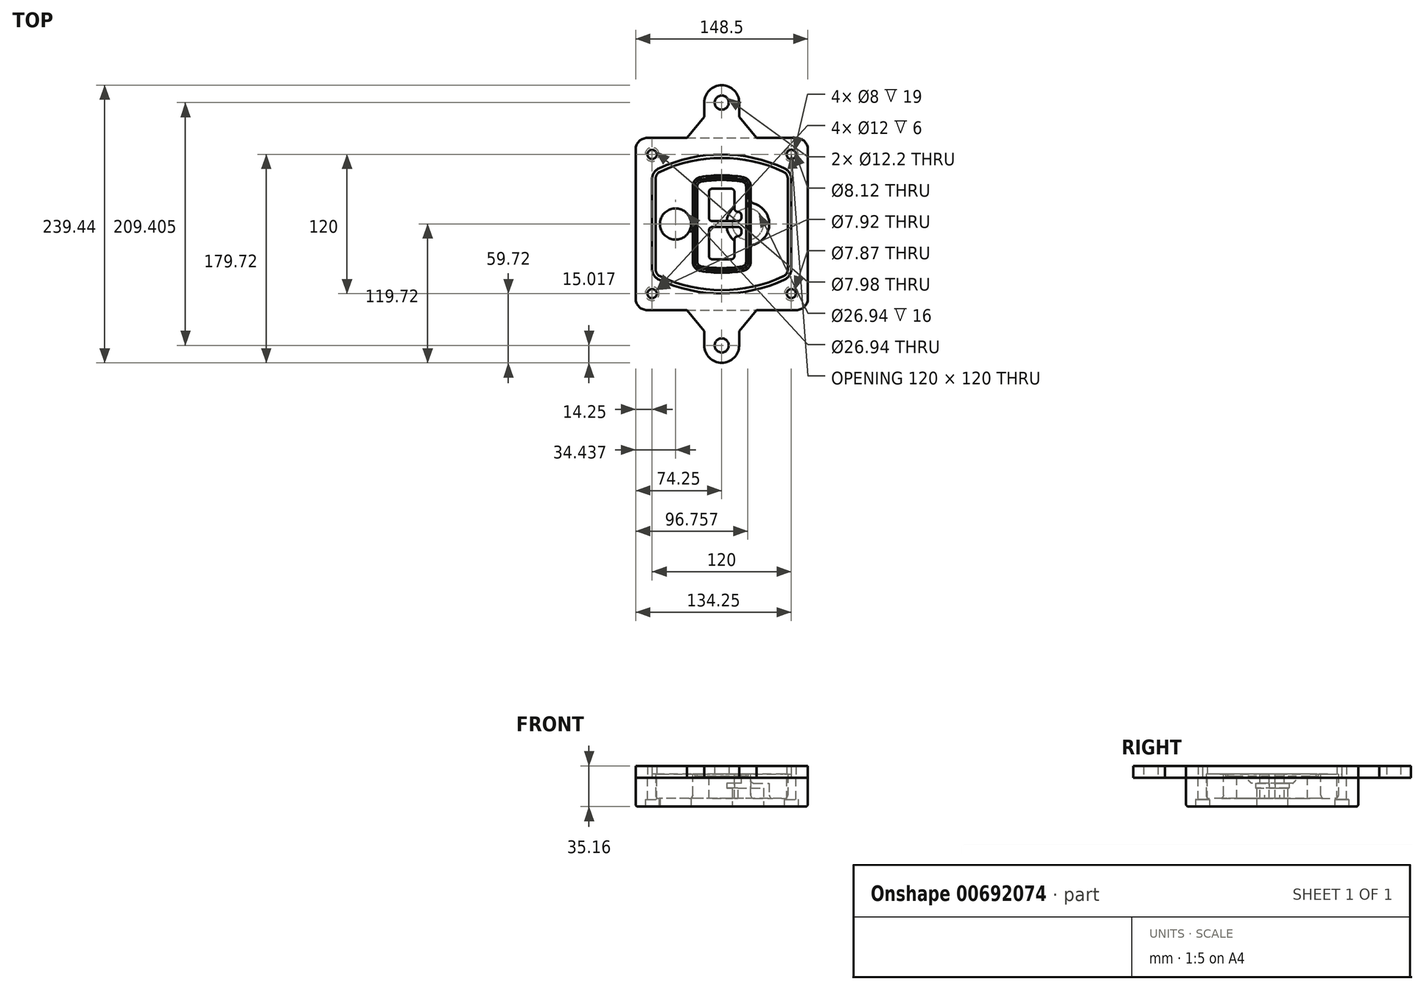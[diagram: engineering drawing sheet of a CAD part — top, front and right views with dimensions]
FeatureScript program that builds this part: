
annotation { "Feature Type Name" : "Feature", "Feature Type Description" : "" }
export const myFeature = defineFeature(function(context is Context, id is Id, definition is map)
    precondition{}
    {
        {
            var Q0;
            Q0=qCreatedBy(makeId("Top.planeOp"),FACE);
            var sketch = newSketch(context, id + "F0", { "sketchPlane" : qUnion([Q0])});
            skPoint(sketch, "E0.rect.middle", {"position": v(0, 0) * mm});
            skLineSegment(sketch, "E1.bottom", {"start": v(-64.25, -74.25) * mm, "end": v(64.25, -74.25) * mm});
            skLineSegment(sketch, "E1.top", {"start": v(-64.25, 74.25) * mm, "end": v(64.25, 74.25) * mm});
            skLineSegment(sketch, "E1.left", {"start": v(-74.25, -64.25) * mm, "end": v(-74.25, 64.25) * mm});
            skLineSegment(sketch, "E1.right", {"start": v(74.25, -64.25) * mm, "end": v(74.25, 64.25) * mm});
            skLineSegment(sketch, "E2", {"start": v(-74.25, 74.25) * mm, "end": v(74.25, -74.25) * mm, "construction": true});
            skLineSegment(sketch, "E3", {"start": v(74.25, 74.25) * mm, "end": v(-74.25, -74.25) * mm, "construction": true});
            skCircle(sketch, "E4", {"center": v(-60, 60) * mm, "radius": 4 * mm});
            skCircle(sketch, "E5", {"center": v(60, 60) * mm, "radius": 4 * mm});
            skCircle(sketch, "E6", {"center": v(60, -60) * mm, "radius": 4 * mm});
            skCircle(sketch, "E7", {"center": v(-60, -60) * mm, "radius": 4 * mm});
            skLineSegment(sketch, "E8", {"start": v(-60, 60) * mm, "end": v(60, 60) * mm, "construction": true});
            skLineSegment(sketch, "E9", {"start": v(60, 60) * mm, "end": v(60, -60) * mm, "construction": true});
            skLineSegment(sketch, "E10", {"start": v(60, -60) * mm, "end": v(-60, -60) * mm, "construction": true});
            skLineSegment(sketch, "E11", {"start": v(-60, -60) * mm, "end": v(-60, 60) * mm, "construction": true});
            skLineSegment(sketch, "E12", {"start": v(-60, 38.83) * mm, "end": v(-60, -38.83) * mm});
            skLineSegment(sketch, "E13", {"start": v(60, 38.83) * mm, "end": v(60, -38.83) * mm});
            skArc(sketch, "E14", {"start": v(54.26, 47.88) * mm, "mid": v(0, 60) * mm, "end": v(-54.26, 47.88) * mm});
            skArc(sketch, "E15", {"start": v(-54.26, -47.88) * mm, "mid": v(0, -60) * mm, "end": v(54.26, -47.88) * mm});
            skLineSegment(sketch, "E16", {"start": v(-60, 0) * mm, "end": v(60, 0) * mm, "construction": true});
            skPoint(sketch, "E17.visualSharp", {"position": v(-60, -45) * mm});
            skArc(sketch, "E17.filletArc", {"start": v(-60, -38.83) * mm, "mid": v(-58.44, -44.2) * mm, "end": v(-54.26, -47.88) * mm});
            skPoint(sketch, "E18.visualSharp", {"position": v(-60, 45) * mm});
            skArc(sketch, "E18.filletArc", {"start": v(-54.26, 47.88) * mm, "mid": v(-58.44, 44.2) * mm, "end": v(-60, 38.83) * mm});
            skPoint(sketch, "E19.visualSharp", {"position": v(60, 45) * mm});
            skArc(sketch, "E19.filletArc", {"start": v(60, 38.83) * mm, "mid": v(58.44, 44.2) * mm, "end": v(54.26, 47.88) * mm});
            skPoint(sketch, "E20.visualSharp", {"position": v(60, -45) * mm});
            skArc(sketch, "E20.filletArc", {"start": v(54.26, -47.88) * mm, "mid": v(58.44, -44.2) * mm, "end": v(60, -38.83) * mm});
            skPoint(sketch, "E21.visualSharp", {"position": v(-74.25, 74.25) * mm});
            skArc(sketch, "E21.filletArc", {"start": v(-64.25, 74.25) * mm, "mid": v(-71.32, 71.32) * mm, "end": v(-74.25, 64.25) * mm});
            skPoint(sketch, "E22.visualSharp", {"position": v(74.25, 74.25) * mm});
            skArc(sketch, "E22.filletArc", {"start": v(74.25, 64.25) * mm, "mid": v(71.32, 71.32) * mm, "end": v(64.25, 74.25) * mm});
            skPoint(sketch, "E23.visualSharp", {"position": v(74.25, -74.25) * mm});
            skArc(sketch, "E23.filletArc", {"start": v(64.25, -74.25) * mm, "mid": v(71.32, -71.32) * mm, "end": v(74.25, -64.25) * mm});
            skPoint(sketch, "E24.visualSharp", {"position": v(-74.25, -74.25) * mm});
            skArc(sketch, "E24.filletArc", {"start": v(-74.25, -64.25) * mm, "mid": v(-71.32, -71.32) * mm, "end": v(-64.25, -74.25) * mm});
            skArc(sketch, "E25.0", {"start": v(57, 38.83) * mm, "mid": v(55.9, 42.58) * mm, "end": v(52.98, 45.17) * mm});
            skLineSegment(sketch, "E25.1", {"start": v(57, 38.83) * mm, "end": v(57, -38.83) * mm});
            skArc(sketch, "E25.2", {"start": v(52.98, -45.17) * mm, "mid": v(55.9, -42.58) * mm, "end": v(57, -38.83) * mm});
            skArc(sketch, "E25.3", {"start": v(-52.98, -45.17) * mm, "mid": v(0, -57) * mm, "end": v(52.98, -45.17) * mm});
            skArc(sketch, "E25.4", {"start": v(-57, -38.83) * mm, "mid": v(-55.9, -42.58) * mm, "end": v(-52.98, -45.17) * mm});
            skArc(sketch, "E25.5", {"start": v(52.98, 45.17) * mm, "mid": v(0, 57) * mm, "end": v(-52.98, 45.17) * mm});
            skLineSegment(sketch, "E25.6", {"start": v(-57, 38.83) * mm, "end": v(-57, -38.83) * mm});
            skArc(sketch, "E25.7", {"start": v(-52.98, 45.17) * mm, "mid": v(-55.9, 42.58) * mm, "end": v(-57, 38.83) * mm});
            skArc(sketch, "E26.0", {"start": v(-55.96, 51.5) * mm, "mid": v(-61.82, 46.33) * mm, "end": v(-64, 38.83) * mm});
            skArc(sketch, "E26.1", {"start": v(55.96, 51.5) * mm, "mid": v(0, 64) * mm, "end": v(-55.96, 51.5) * mm});
            skArc(sketch, "E26.2", {"start": v(64, 38.83) * mm, "mid": v(61.82, 46.33) * mm, "end": v(55.96, 51.5) * mm});
            skLineSegment(sketch, "E26.3", {"start": v(64, 38.83) * mm, "end": v(64, -38.83) * mm});
            skArc(sketch, "E26.4", {"start": v(55.96, -51.5) * mm, "mid": v(61.82, -46.33) * mm, "end": v(64, -38.83) * mm});
            skLineSegment(sketch, "E26.5", {"start": v(-64, 38.83) * mm, "end": v(-64, -38.83) * mm});
            skArc(sketch, "E26.6", {"start": v(-55.96, -51.5) * mm, "mid": v(0, -64) * mm, "end": v(55.96, -51.5) * mm});
            skArc(sketch, "E26.7", {"start": v(-64, -38.83) * mm, "mid": v(-61.82, -46.33) * mm, "end": v(-55.96, -51.5) * mm});
            skSolve(sketch);
        }
        {
            var Q0;
            Q0=makeQuery(id+"F0.imprint","IMPRINT",FACE,{"disambiguationData":[TD([[makeQuery(id+"F0.imprint","IMPRINT",EDGE,{"derivedFrom":sQuery(id+"F0.wireOp",EDGE,"E1.bottom")}),1.0]])]});
            var Q1;
            Q1=makeQuery(id+"F0.imprint","IMPRINT",FACE,{"disambiguationData":[TD([[makeQuery(id+"F0.imprint","IMPRINT",EDGE,{"derivedFrom":sQuery(id+"F0.wireOp",EDGE,"E12")}),1.0]])]});
            var Q2;
            Q2=makeQuery(id+"F0.imprint","IMPRINT",FACE,{"disambiguationData":[TD([[makeQuery(id+"F0.imprint","IMPRINT",EDGE,{"derivedFrom":sQuery(id+"F0.wireOp",EDGE,"E25.0")}),1.0]])]});
            var Q3;
            Q3=makeQuery(id+"F0.imprint","IMPRINT",FACE,{"disambiguationData":[TD([[makeQuery(id+"F0.imprint","IMPRINT",EDGE,{"derivedFrom":sQuery(id+"F0.wireOp",EDGE,"E12")}),-1.0]])]});
            extrude(context, id + "F1", {"entities" : qUnion([Q0, Q1, Q2, Q3]), "oppositeDirection" : true, "depth" : 25 * mm});
        }
        {
            var Q0;
            Q0=makeQuery(id+"F0.imprint","IMPRINT",FACE,{"disambiguationData":[TD([[makeQuery(id+"F0.imprint","IMPRINT",EDGE,{"derivedFrom":sQuery(id+"F0.wireOp",EDGE,"E12")}),1.0]])]});
            extrude(context, id + "F2", {"entities" : qUnion([Q0]), "operationType" : NewBodyOperationType.ADD, "depth" : 3 * mm});
        }
        {
            var Q0;
            Q0=makeQuery(id+"F0.imprint","IMPRINT",FACE,{"disambiguationData":[TD([[makeQuery(id+"F0.imprint","IMPRINT",EDGE,{"derivedFrom":sQuery(id+"F0.wireOp",EDGE,"E25.0")}),1.0]])]});
            extrude(context, id + "F3", {"entities" : qUnion([Q0]), "operationType" : NewBodyOperationType.REMOVE, "oppositeDirection" : true, "depth" : 18 * mm});
        }
        {
            var Q0;
            Q0=makeQuery(id+"F2.opExtrude","CAP_FACE",FACE,{"disambiguationData":[OSD([sQuery(id+"F0.wireOp",EDGE,"E12"),sQuery(id+"F0.wireOp",EDGE,"E13"),sQuery(id+"F0.wireOp",EDGE,"E14"),sQuery(id+"F0.wireOp",EDGE,"E15"),sQuery(id+"F0.wireOp",EDGE,"E17.filletArc"),sQuery(id+"F0.wireOp",EDGE,"E18.filletArc"),sQuery(id+"F0.wireOp",EDGE,"E19.filletArc"),sQuery(id+"F0.wireOp",EDGE,"E20.filletArc"),sQuery(id+"F0.wireOp",EDGE,"E25.0"),sQuery(id+"F0.wireOp",EDGE,"E25.1"),sQuery(id+"F0.wireOp",EDGE,"E25.2"),sQuery(id+"F0.wireOp",EDGE,"E25.3"),sQuery(id+"F0.wireOp",EDGE,"E25.4"),sQuery(id+"F0.wireOp",EDGE,"E25.5"),sQuery(id+"F0.wireOp",EDGE,"E25.6"),sQuery(id+"F0.wireOp",EDGE,"E25.7")])],"isStart":false});
            var sketch = newSketch(context, id + "F4", { "sketchPlane" : qUnion([Q0])});
            skArc(sketch, "E27.0", {"start": v(-18.34, -40.45) * mm, "mid": v(0, -42) * mm, "end": v(18.34, -40.45) * mm});
            skArc(sketch, "E28.0", {"start": v(18.34, 40.45) * mm, "mid": v(0, 42) * mm, "end": v(-18.34, 40.45) * mm});
            skLineSegment(sketch, "E29", {"start": v(-25, 32.57) * mm, "end": v(-25, -32.57) * mm});
            skLineSegment(sketch, "E30", {"start": v(25, 32.57) * mm, "end": v(25, -32.57) * mm});
            skLineSegment(sketch, "E31", {"start": v(-25, 39.1) * mm, "end": v(25, 39.1) * mm, "construction": true});
            skLineSegment(sketch, "E32", {"start": v(-25, -39.1) * mm, "end": v(25, -39.1) * mm, "construction": true});
            skPoint(sketch, "E33.visualSharp", {"position": v(-25, 39.1) * mm});
            skArc(sketch, "E33.filletArc", {"start": v(-18.34, 40.45) * mm, "mid": v(-23.11, 37.73) * mm, "end": v(-25, 32.57) * mm});
            skPoint(sketch, "E34.visualSharp", {"position": v(25, 39.1) * mm});
            skArc(sketch, "E34.filletArc", {"start": v(25, 32.57) * mm, "mid": v(23.11, 37.73) * mm, "end": v(18.34, 40.45) * mm});
            skPoint(sketch, "E35.visualSharp", {"position": v(25, -39.1) * mm});
            skArc(sketch, "E35.filletArc", {"start": v(18.34, -40.45) * mm, "mid": v(23.11, -37.73) * mm, "end": v(25, -32.57) * mm});
            skPoint(sketch, "E36.visualSharp", {"position": v(-25, -39.1) * mm});
            skArc(sketch, "E36.filletArc", {"start": v(-25, -32.57) * mm, "mid": v(-23.11, -37.73) * mm, "end": v(-18.34, -40.45) * mm});
            skArc(sketch, "E37.0", {"start": v(52.98, 45.17) * mm, "mid": v(0, 57) * mm, "end": v(-52.98, 45.17) * mm});
            skArc(sketch, "E37.1", {"start": v(-52.98, 45.17) * mm, "mid": v(-55.9, 42.58) * mm, "end": v(-57, 38.83) * mm});
            skLineSegment(sketch, "E37.2", {"start": v(-57, 38.83) * mm, "end": v(-57, -38.83) * mm});
            skArc(sketch, "E37.3", {"start": v(-57, -38.83) * mm, "mid": v(-55.9, -42.58) * mm, "end": v(-52.98, -45.17) * mm});
            skArc(sketch, "E37.4", {"start": v(-52.98, -45.17) * mm, "mid": v(0, -57) * mm, "end": v(52.98, -45.17) * mm});
            skArc(sketch, "E37.5", {"start": v(52.98, -45.17) * mm, "mid": v(55.9, -42.58) * mm, "end": v(57, -38.83) * mm});
            skLineSegment(sketch, "E37.6", {"start": v(57, 38.83) * mm, "end": v(57, -38.83) * mm});
            skArc(sketch, "E37.7", {"start": v(57, 38.83) * mm, "mid": v(55.9, 42.58) * mm, "end": v(52.98, 45.17) * mm});
            skLineSegment(sketch, "E38.0", {"start": v(23, 32.57) * mm, "end": v(23, -32.57) * mm});
            skArc(sketch, "E38.1", {"start": v(18, -38.48) * mm, "mid": v(21.58, -36.44) * mm, "end": v(23, -32.57) * mm});
            skArc(sketch, "E38.2", {"start": v(-18, -38.48) * mm, "mid": v(0, -40) * mm, "end": v(18, -38.48) * mm});
            skArc(sketch, "E38.3", {"start": v(-23, -32.57) * mm, "mid": v(-21.58, -36.44) * mm, "end": v(-18, -38.48) * mm});
            skLineSegment(sketch, "E38.4", {"start": v(-23, 32.57) * mm, "end": v(-23, -32.57) * mm});
            skArc(sketch, "E38.5", {"start": v(23, 32.57) * mm, "mid": v(21.58, 36.44) * mm, "end": v(18, 38.48) * mm});
            skArc(sketch, "E38.6", {"start": v(-18, 38.48) * mm, "mid": v(-21.58, 36.44) * mm, "end": v(-23, 32.57) * mm});
            skArc(sketch, "E38.7", {"start": v(18, 38.48) * mm, "mid": v(0, 40) * mm, "end": v(-18, 38.48) * mm});
            skArc(sketch, "E39.0", {"start": v(21, 32.57) * mm, "mid": v(20.06, 35.15) * mm, "end": v(17.67, 36.5) * mm});
            skLineSegment(sketch, "E39.1", {"start": v(21, 32.57) * mm, "end": v(21, -32.57) * mm});
            skArc(sketch, "E39.2", {"start": v(17.67, -36.5) * mm, "mid": v(20.06, -35.15) * mm, "end": v(21, -32.57) * mm});
            skArc(sketch, "E39.3", {"start": v(-17.67, -36.5) * mm, "mid": v(0, -38) * mm, "end": v(17.67, -36.5) * mm});
            skArc(sketch, "E39.4", {"start": v(-21, -32.57) * mm, "mid": v(-20.06, -35.15) * mm, "end": v(-17.67, -36.5) * mm});
            skArc(sketch, "E39.5", {"start": v(17.67, 36.5) * mm, "mid": v(0, 38) * mm, "end": v(-17.67, 36.5) * mm});
            skLineSegment(sketch, "E39.6", {"start": v(-21, 32.57) * mm, "end": v(-21, -32.57) * mm});
            skArc(sketch, "E39.7", {"start": v(-17.67, 36.5) * mm, "mid": v(-20.06, 35.15) * mm, "end": v(-21, 32.57) * mm});
            skLineSegment(sketch, "E40", {"start": v(-25, 0) * mm, "end": v(25, 0) * mm, "construction": true});
            skLineSegment(sketch, "E41", {"start": v(-11, 5.5) * mm, "end": v(-11, 27.5) * mm});
            skLineSegment(sketch, "E42", {"start": v(-8, 30.5) * mm, "end": v(8, 30.5) * mm});
            skLineSegment(sketch, "E43", {"start": v(11, 27.5) * mm, "end": v(11, 13.5) * mm});
            skLineSegment(sketch, "E44", {"start": v(14, 10.5) * mm, "end": v(14, 10.5) * mm});
            skLineSegment(sketch, "E45", {"start": v(17, 7.5) * mm, "end": v(17, 5.5) * mm});
            skLineSegment(sketch, "E46", {"start": v(14, 2.5) * mm, "end": v(-8, 2.5) * mm});
            skPoint(sketch, "E47.visualSharp", {"position": v(-11, 30.5) * mm});
            skArc(sketch, "E47.filletArc", {"start": v(-8, 30.5) * mm, "mid": v(-10.12, 29.62) * mm, "end": v(-11, 27.5) * mm});
            skPoint(sketch, "E48.visualSharp", {"position": v(11, 30.5) * mm});
            skArc(sketch, "E48.filletArc", {"start": v(11, 27.5) * mm, "mid": v(10.12, 29.62) * mm, "end": v(8, 30.5) * mm});
            skPoint(sketch, "E49.visualSharp", {"position": v(11, 10.5) * mm});
            skArc(sketch, "E49.filletArc", {"start": v(11, 13.5) * mm, "mid": v(11.88, 11.38) * mm, "end": v(14, 10.5) * mm});
            skPoint(sketch, "E50.visualSharp", {"position": v(17, 10.5) * mm});
            skArc(sketch, "E50.filletArc", {"start": v(17, 7.5) * mm, "mid": v(16.12, 9.62) * mm, "end": v(14, 10.5) * mm});
            skPoint(sketch, "E51.visualSharp", {"position": v(17, 2.5) * mm});
            skArc(sketch, "E51.filletArc", {"start": v(14, 2.5) * mm, "mid": v(16.12, 3.38) * mm, "end": v(17, 5.5) * mm});
            skPoint(sketch, "E52.visualSharp", {"position": v(-11, 2.5) * mm});
            skArc(sketch, "E52.filletArc", {"start": v(-11, 5.5) * mm, "mid": v(-10.12, 3.38) * mm, "end": v(-8, 2.5) * mm});
            skLineSegment(sketch, "E53.0.MirrorCS", {"start": v(14, -2.5) * mm, "end": v(-8, -2.5) * mm});
            skArc(sketch, "E54.0.MirrorCS", {"start": v(-11, -5.5) * mm, "mid": v(-10.12, -3.38) * mm, "end": v(-8, -2.5) * mm});
            skLineSegment(sketch, "E55.0.MirrorCS", {"start": v(-11, -5.5) * mm, "end": v(-11, -27.5) * mm});
            skArc(sketch, "E56.0.MirrorCS", {"start": v(-8, -30.5) * mm, "mid": v(-10.12, -29.62) * mm, "end": v(-11, -27.5) * mm});
            skLineSegment(sketch, "E57.0.MirrorCS", {"start": v(-8, -30.5) * mm, "end": v(8, -30.5) * mm});
            skArc(sketch, "E58.0.MirrorCS", {"start": v(11, -27.5) * mm, "mid": v(10.12, -29.62) * mm, "end": v(8, -30.5) * mm});
            skLineSegment(sketch, "E59.0.MirrorCS", {"start": v(11, -27.5) * mm, "end": v(11, -13.5) * mm});
            skArc(sketch, "E60.0.MirrorCS", {"start": v(11, -13.5) * mm, "mid": v(11.88, -11.38) * mm, "end": v(14, -10.5) * mm});
            skArc(sketch, "E61.0.MirrorCS", {"start": v(17, -7.5) * mm, "mid": v(16.12, -9.62) * mm, "end": v(14, -10.5) * mm});
            skLineSegment(sketch, "E62.0.MirrorCS", {"start": v(17, -7.5) * mm, "end": v(17, -5.5) * mm});
            skArc(sketch, "E63.0.MirrorCS", {"start": v(14, -2.5) * mm, "mid": v(16.12, -3.38) * mm, "end": v(17, -5.5) * mm});
            skSolve(sketch);
        }
        {
            var Q0;
            Q0=makeQuery(id+"F4.imprint","IMPRINT",FACE,{"disambiguationData":[TD([[makeQuery(id+"F4.imprint","IMPRINT",EDGE,{"derivedFrom":sQuery(id+"F4.wireOp",EDGE,"E27.0")}),1.0]])]});
            var Q1;
            Q1=makeQuery(id+"F4.imprint","IMPRINT",FACE,{"disambiguationData":[TD([[makeQuery(id+"F4.imprint","IMPRINT",EDGE,{"derivedFrom":sQuery(id+"F4.wireOp",EDGE,"E38.0")}),-1.0]])]});
            var Q2;
            Q2=makeQuery(id+"F4.imprint","IMPRINT",FACE,{"disambiguationData":[TD([[makeQuery(id+"F4.imprint","IMPRINT",EDGE,{"derivedFrom":sQuery(id+"F4.wireOp",EDGE,"E39.0")}),1.0]])]});
            extrude(context, id + "F5", {"entities" : qUnion([Q0, Q1, Q2]), "operationType" : NewBodyOperationType.ADD, "endBound" : BoundingType.UP_TO_NEXT, "oppositeDirection" : true, "depth" : 25 * mm});
        }
        {
            var Q0;
            Q0=makeQuery(id+"F4.imprint","IMPRINT",FACE,{"disambiguationData":[TD([[makeQuery(id+"F4.imprint","IMPRINT",EDGE,{"derivedFrom":sQuery(id+"F4.wireOp",EDGE,"E38.0")}),-1.0]])]});
            extrude(context, id + "F6", {"entities" : qUnion([Q0]), "operationType" : NewBodyOperationType.REMOVE, "oppositeDirection" : true, "depth" : 2 * mm});
        }
        {
            var Q0;
            Q0=makeQuery(id+"F1.opExtrude","CAP_FACE",FACE,{"disambiguationData":[OSD([sQuery(id+"F0.wireOp",EDGE,"E1.bottom"),sQuery(id+"F0.wireOp",EDGE,"E1.top"),sQuery(id+"F0.wireOp",EDGE,"E1.left"),sQuery(id+"F0.wireOp",EDGE,"E1.right"),sQuery(id+"F0.wireOp",EDGE,"E4"),sQuery(id+"F0.wireOp",EDGE,"E5"),sQuery(id+"F0.wireOp",EDGE,"E6"),sQuery(id+"F0.wireOp",EDGE,"E7"),sQuery(id+"F0.wireOp",EDGE,"E21.filletArc"),sQuery(id+"F0.wireOp",EDGE,"E22.filletArc"),sQuery(id+"F0.wireOp",EDGE,"E23.filletArc"),sQuery(id+"F0.wireOp",EDGE,"E24.filletArc")])],"isStart":false});
            var sketch = newSketch(context, id + "F7", { "sketchPlane" : qUnion([Q0])});
            skCircle(sketch, "E64", {"center": v(22.5, 0) * mm, "radius": 13.47 * mm});
            skCircle(sketch, "E65", {"center": v(-39.81, 0) * mm, "radius": 13.47 * mm});
            skLineSegment(sketch, "E66", {"start": v(74.25, 0) * mm, "end": v(-74.25, 0) * mm});
            skCircle(sketch, "E67", {"center": v(22.5, 0) * mm, "radius": 18.47 * mm});
            skCircle(sketch, "E68", {"center": v(60, -60) * mm, "radius": 6 * mm});
            skCircle(sketch, "E69", {"center": v(-60, -60) * mm, "radius": 6 * mm});
            skCircle(sketch, "E70", {"center": v(-60, 60) * mm, "radius": 6 * mm});
            skCircle(sketch, "E71", {"center": v(60, 60) * mm, "radius": 6 * mm});
            skSolve(sketch);
        }
        {
            var Q0;
            {var subQ1=sQuery(id+"F7.wireOp",EDGE,"E66");var subQ4=sQuery(id+"F7.wireOp",EDGE,"E64");var subQ6=makeQuery(id+"F7.imprint","INTERSECT",VERTEX,{"disambiguationData":[OD(0.0)],"derivedFrom":[subQ4,subQ1]});Q0=makeQuery(id+"F7.imprint","IMPRINT",FACE,{"disambiguationData":[TD([[makeQuery(id+"F7.imprint","IMPRINT",EDGE,{"disambiguationData":[TD([[subQ6,-1.0]])],"derivedFrom":subQ4}),-1.0]])]});}
            var Q1;
            {var subQ0=sQuery(id+"F7.wireOp",EDGE,"E66");var subQ1=sQuery(id+"F7.wireOp",EDGE,"E64");var subQ3=makeQuery(id+"F7.imprint","INTERSECT",VERTEX,{"disambiguationData":[OD(0.0)],"derivedFrom":[subQ1,subQ0]});Q1=makeQuery(id+"F7.imprint","IMPRINT",FACE,{"disambiguationData":[TD([[makeQuery(id+"F7.imprint","IMPRINT",EDGE,{"disambiguationData":[TD([[subQ3,-1.0]])],"derivedFrom":subQ1}),1.0]])]});}
            var Q2;
            {var subQ0=sQuery(id+"F7.wireOp",EDGE,"E66");var subQ1=sQuery(id+"F7.wireOp",EDGE,"E64");var subQ3=makeQuery(id+"F7.imprint","INTERSECT",VERTEX,{"disambiguationData":[OD(0.0)],"derivedFrom":[subQ1,subQ0]});Q2=makeQuery(id+"F7.imprint","IMPRINT",FACE,{"disambiguationData":[TD([[makeQuery(id+"F7.imprint","IMPRINT",EDGE,{"disambiguationData":[TD([[subQ3,1.0]])],"derivedFrom":subQ1}),1.0]])]});}
            var Q3;
            {var subQ1=sQuery(id+"F7.wireOp",EDGE,"E66");var subQ4=sQuery(id+"F7.wireOp",EDGE,"E64");var subQ6=makeQuery(id+"F7.imprint","INTERSECT",VERTEX,{"disambiguationData":[OD(0.0)],"derivedFrom":[subQ4,subQ1]});Q3=makeQuery(id+"F7.imprint","IMPRINT",FACE,{"disambiguationData":[TD([[makeQuery(id+"F7.imprint","IMPRINT",EDGE,{"disambiguationData":[TD([[subQ6,1.0]])],"derivedFrom":subQ4}),-1.0]])]});}
            extrude(context, id + "F8", {"entities" : qUnion([Q0, Q1, Q2, Q3]), "operationType" : NewBodyOperationType.ADD, "oppositeDirection" : true, "depth" : 20 * mm});
        }
        {
            var Q0;
            {var subQ0=sQuery(id+"F7.wireOp",EDGE,"E66");var subQ1=sQuery(id+"F7.wireOp",EDGE,"E64");var subQ3=makeQuery(id+"F7.imprint","INTERSECT",VERTEX,{"disambiguationData":[OD(0.0)],"derivedFrom":[subQ1,subQ0]});Q0=makeQuery(id+"F7.imprint","IMPRINT",FACE,{"disambiguationData":[TD([[makeQuery(id+"F7.imprint","IMPRINT",EDGE,{"disambiguationData":[TD([[subQ3,-1.0]])],"derivedFrom":subQ1}),1.0]])]});}
            var Q1;
            {var subQ0=sQuery(id+"F7.wireOp",EDGE,"E66");var subQ1=sQuery(id+"F7.wireOp",EDGE,"E64");var subQ3=makeQuery(id+"F7.imprint","INTERSECT",VERTEX,{"disambiguationData":[OD(0.0)],"derivedFrom":[subQ1,subQ0]});Q1=makeQuery(id+"F7.imprint","IMPRINT",FACE,{"disambiguationData":[TD([[makeQuery(id+"F7.imprint","IMPRINT",EDGE,{"disambiguationData":[TD([[subQ3,1.0]])],"derivedFrom":subQ1}),1.0]])]});}
            extrude(context, id + "F9", {"entities" : qUnion([Q0, Q1]), "operationType" : NewBodyOperationType.REMOVE, "oppositeDirection" : true, "depth" : 16 * mm});
        }
        {
            var Q0;
            {var subQ0=sQuery(id+"F7.wireOp",EDGE,"E66");var subQ1=sQuery(id+"F7.wireOp",EDGE,"E65");var subQ3=makeQuery(id+"F7.imprint","INTERSECT",VERTEX,{"disambiguationData":[OD(0.0)],"derivedFrom":[subQ1,subQ0]});Q0=makeQuery(id+"F7.imprint","IMPRINT",FACE,{"disambiguationData":[TD([[makeQuery(id+"F7.imprint","IMPRINT",EDGE,{"disambiguationData":[TD([[subQ3,-1.0]])],"derivedFrom":subQ1}),1.0]])]});}
            var Q1;
            {var subQ0=sQuery(id+"F7.wireOp",EDGE,"E66");var subQ1=sQuery(id+"F7.wireOp",EDGE,"E65");var subQ3=makeQuery(id+"F7.imprint","INTERSECT",VERTEX,{"disambiguationData":[OD(0.0)],"derivedFrom":[subQ1,subQ0]});Q1=makeQuery(id+"F7.imprint","IMPRINT",FACE,{"disambiguationData":[TD([[makeQuery(id+"F7.imprint","IMPRINT",EDGE,{"disambiguationData":[TD([[subQ3,1.0]])],"derivedFrom":subQ1}),1.0]])]});}
            extrude(context, id + "F10", {"entities" : qUnion([Q0, Q1]), "operationType" : NewBodyOperationType.REMOVE, "oppositeDirection" : true, "depth" : 25 * mm});
        }
        {
            var Q0;
            Q0=makeQuery(id+"F7.imprint","IMPRINT",FACE,{"disambiguationData":[TD([[makeQuery(id+"F7.imprint","IMPRINT",EDGE,{"derivedFrom":sQuery(id+"F7.wireOp",EDGE,"E68")}),1.0]])]});
            var Q1;
            Q1=makeQuery(id+"F7.imprint","IMPRINT",FACE,{"disambiguationData":[TD([[makeQuery(id+"F7.imprint","IMPRINT",EDGE,{"derivedFrom":makeQuery(id+"F1.opExtrude","CAP_EDGE",EDGE,{"disambiguationData":[OSD([sQuery(id+"F0.wireOp",EDGE,"E5")])],"isStart":false})}),-1.0]])]});
            var Q2;
            Q2=makeQuery(id+"F7.imprint","IMPRINT",FACE,{"disambiguationData":[TD([[makeQuery(id+"F7.imprint","IMPRINT",EDGE,{"derivedFrom":sQuery(id+"F7.wireOp",EDGE,"E69")}),1.0]])]});
            var Q3;
            Q3=makeQuery(id+"F7.imprint","IMPRINT",FACE,{"disambiguationData":[TD([[makeQuery(id+"F7.imprint","IMPRINT",EDGE,{"derivedFrom":makeQuery(id+"F1.opExtrude","CAP_EDGE",EDGE,{"disambiguationData":[OSD([sQuery(id+"F0.wireOp",EDGE,"E4")])],"isStart":false})}),-1.0]])]});
            var Q4;
            Q4=makeQuery(id+"F7.imprint","IMPRINT",FACE,{"disambiguationData":[TD([[makeQuery(id+"F7.imprint","IMPRINT",EDGE,{"derivedFrom":sQuery(id+"F7.wireOp",EDGE,"E70")}),1.0]])]});
            var Q5;
            Q5=makeQuery(id+"F7.imprint","IMPRINT",FACE,{"disambiguationData":[TD([[makeQuery(id+"F7.imprint","IMPRINT",EDGE,{"derivedFrom":makeQuery(id+"F1.opExtrude","CAP_EDGE",EDGE,{"disambiguationData":[OSD([sQuery(id+"F0.wireOp",EDGE,"E7")])],"isStart":false})}),-1.0]])]});
            var Q6;
            Q6=makeQuery(id+"F7.imprint","IMPRINT",FACE,{"disambiguationData":[TD([[makeQuery(id+"F7.imprint","IMPRINT",EDGE,{"derivedFrom":sQuery(id+"F7.wireOp",EDGE,"E71")}),1.0]])]});
            var Q7;
            Q7=makeQuery(id+"F7.imprint","IMPRINT",FACE,{"disambiguationData":[TD([[makeQuery(id+"F7.imprint","IMPRINT",EDGE,{"derivedFrom":makeQuery(id+"F1.opExtrude","CAP_EDGE",EDGE,{"disambiguationData":[OSD([sQuery(id+"F0.wireOp",EDGE,"E6")])],"isStart":false})}),-1.0]])]});
            extrude(context, id + "F11", {"entities" : qUnion([Q0, Q1, Q2, Q3, Q4, Q5, Q6, Q7]), "operationType" : NewBodyOperationType.REMOVE, "oppositeDirection" : true, "depth" : 6 * mm});
        }
        {
            var Q0;
            Q0=makeQuery(id+"F9.boolean.opBoolean","COPY",FACE,{"derivedFrom":makeQuery(id+"F9.opExtrude","CAP_FACE",FACE,{"disambiguationData":[OSD([sQuery(id+"F7.wireOp",EDGE,"E64")])],"isStart":false})});
            var sketch = newSketch(context, id + "F12", { "sketchPlane" : qUnion([Q0])});
            skArc(sketch, "E72.0", {"start": v(11, 14.45) * mm, "mid": v(6.45, 9.13) * mm, "end": v(4.2, 2.5) * mm});
            skArc(sketch, "E72.1", {"start": v(4.2, -2.5) * mm, "mid": v(6.45, -9.13) * mm, "end": v(11, -14.45) * mm});
            skLineSegment(sketch, "E73", {"start": v(4.2, -2.5) * mm, "end": v(14, -2.5) * mm});
            skLineSegment(sketch, "E74.0", {"start": v(14, 2.5) * mm, "end": v(4.2, 2.5) * mm});
            skArc(sketch, "E74.1", {"start": v(14, 2.5) * mm, "mid": v(16.12, 3.38) * mm, "end": v(17, 5.5) * mm});
            skLineSegment(sketch, "E74.2", {"start": v(17, 7.5) * mm, "end": v(17, 5.5) * mm});
            skArc(sketch, "E74.3", {"start": v(17, 7.5) * mm, "mid": v(16.12, 9.62) * mm, "end": v(14, 10.5) * mm});
            skArc(sketch, "E74.4", {"start": v(11, 13.5) * mm, "mid": v(11.88, 11.38) * mm, "end": v(14, 10.5) * mm});
            skLineSegment(sketch, "E74.5", {"start": v(11, 14.45) * mm, "end": v(11, 13.5) * mm});
            skLineSegment(sketch, "E74.7", {"start": v(14, -2.5) * mm, "end": v(4.2, -2.5) * mm});
            skArc(sketch, "E74.8", {"start": v(14, -2.5) * mm, "mid": v(16.12, -3.38) * mm, "end": v(17, -5.5) * mm});
            skLineSegment(sketch, "E74.9", {"start": v(17, -7.5) * mm, "end": v(17, -5.5) * mm});
            skArc(sketch, "E74.10", {"start": v(17, -7.5) * mm, "mid": v(16.12, -9.62) * mm, "end": v(14, -10.5) * mm});
            skArc(sketch, "E74.11", {"start": v(11, -13.5) * mm, "mid": v(11.88, -11.38) * mm, "end": v(14, -10.5) * mm});
            skLineSegment(sketch, "E74.12", {"start": v(11, -14.45) * mm, "end": v(11, -13.5) * mm});
            skPoint(sketch, "E75.orphan", {"position": v(11, -27.5) * mm});
            skPoint(sketch, "E76.orphan", {"position": v(-8, -2.5) * mm});
            skPoint(sketch, "E77.orphan", {"position": v(-8, 2.5) * mm});
            skPoint(sketch, "E78.orphan", {"position": v(11, 27.5) * mm});
            skSolve(sketch);
        }
        {
            var Q0;
            {var subQ7=sQuery(id+"F12.wireOp",EDGE,"E72.0");var subQ14=sQuery(id+"F12.wireOp",EDGE,"E72.1");var subQ16=sQuery(id+"F12.wireOp",EDGE,"E74.1");var subQ18=sQuery(id+"F12.wireOp",EDGE,"E74.8");Q0=qUnion([makeQuery(id+"F12.imprint","IMPRINT",FACE,{"disambiguationData":[TD([[makeQuery(id+"F12.imprint","IMPRINT",EDGE,{"derivedFrom":subQ7}),1.0]])]}),makeQuery(id+"F12.imprint","IMPRINT",FACE,{"disambiguationData":[TD([[makeQuery(id+"F12.imprint","IMPRINT",EDGE,{"derivedFrom":subQ14}),1.0]])]}),makeQuery(id+"F12.imprint","IMPRINT",FACE,{"disambiguationData":[TD([[makeQuery(id+"F12.imprint","IMPRINT",EDGE,{"derivedFrom":subQ16}),1.0]])]}),makeQuery(id+"F12.imprint","IMPRINT",FACE,{"disambiguationData":[TD([[makeQuery(id+"F12.imprint","IMPRINT",EDGE,{"derivedFrom":subQ18}),-1.0]])]})]);}
            var Q1;
            Q1=makeQuery(id+"F5.boolean.opBoolean","SPLIT",FACE,{"disambiguationData":[TD([makeQuery(id+"F5.opExtrude","SWEPT_FACE",FACE,{"disambiguationData":[OSD([sQuery(id+"F4.wireOp",EDGE,"E41")])]})])],"derivedFrom":makeQuery(id+"F3.boolean.opBoolean","COPY",FACE,{"derivedFrom":makeQuery(id+"F3.opExtrude","CAP_FACE",FACE,{"disambiguationData":[OSD([sQuery(id+"F0.wireOp",EDGE,"E25.0"),sQuery(id+"F0.wireOp",EDGE,"E25.1"),sQuery(id+"F0.wireOp",EDGE,"E25.2"),sQuery(id+"F0.wireOp",EDGE,"E25.3"),sQuery(id+"F0.wireOp",EDGE,"E25.4"),sQuery(id+"F0.wireOp",EDGE,"E25.5"),sQuery(id+"F0.wireOp",EDGE,"E25.6"),sQuery(id+"F0.wireOp",EDGE,"E25.7")])],"isStart":false})})});
            extrude(context, id + "F13", {"entities" : qUnion([Q0]), "operationType" : NewBodyOperationType.REMOVE, "endBound" : BoundingType.UP_TO_SURFACE, "endBoundEntityFace" : qUnion([Q1]), "depth" : 25 * mm});
        }
        {
            var Q0;
            Q0=makeQuery(id+"F3.boolean.opBoolean","COPY",EDGE,{"derivedFrom":makeQuery(id+"F3.opExtrude","CAP_EDGE",EDGE,{"disambiguationData":[OSD([sQuery(id+"F0.wireOp",EDGE,"E25.6")])],"isStart":false})});
            var Q1;
            Q1=makeQuery(id+"F8.boolean.opBoolean","INTERSECT",EDGE,{"derivedFrom":[makeQuery(id+"F5.opExtrude","SWEPT_FACE",FACE,{"disambiguationData":[OSD([sQuery(id+"F4.wireOp",EDGE,"E30")])]}),makeQuery(id+"F8.opExtrude","CAP_FACE",FACE,{"disambiguationData":[OSD([sQuery(id+"F7.wireOp",EDGE,"E67")])],"isStart":false})]});
            var Q2;
            Q2=makeQuery(id+"F8.boolean.opBoolean","INTERSECT",EDGE,{"disambiguationData":[OD(1.0)],"derivedFrom":[makeQuery(id+"F5.opExtrude","SWEPT_FACE",FACE,{"disambiguationData":[OSD([sQuery(id+"F4.wireOp",EDGE,"E30")])]}),makeQuery(id+"F8.opExtrude","SWEPT_FACE",FACE,{"disambiguationData":[OSD([sQuery(id+"F7.wireOp",EDGE,"E67")])]})]});
            var Q3;
            {var subQ0=sQuery(id+"F4.wireOp",EDGE,"E30");Q3=makeQuery(id+"F8.boolean.opBoolean","SPLIT",EDGE,{"disambiguationData":[TD([makeQuery(id+"F5.opExtrude","SWEPT_FACE",FACE,{"disambiguationData":[OSD([sQuery(id+"F4.wireOp",EDGE,"E35.filletArc")])]})])],"derivedFrom":makeQuery(id+"F5.opExtrude","CAP_EDGE",EDGE,{"disambiguationData":[OSD([subQ0])],"isStart":false})});}
            var Q4;
            {var subQ0=sQuery(id+"F0.wireOp",EDGE,"E25.7");var subQ1=sQuery(id+"F0.wireOp",EDGE,"E25.1");var subQ2=sQuery(id+"F0.wireOp",EDGE,"E25.6");var subQ3=sQuery(id+"F0.wireOp",EDGE,"E25.5");var subQ4=sQuery(id+"F0.wireOp",EDGE,"E25.4");var subQ5=sQuery(id+"F0.wireOp",EDGE,"E25.0");var subQ6=sQuery(id+"F0.wireOp",EDGE,"E25.2");var subQ7=sQuery(id+"F0.wireOp",EDGE,"E25.3");Q4=makeQuery(id+"F8.boolean.opBoolean","INTERSECT",EDGE,{"derivedFrom":[makeQuery(id+"F5.boolean.opBoolean","SPLIT",FACE,{"disambiguationData":[TD([makeQuery(id+"F2.opExtrude","SWEPT_FACE",FACE,{"disambiguationData":[OSD([subQ5])]})])],"derivedFrom":makeQuery(id+"F3.boolean.opBoolean","COPY",FACE,{"derivedFrom":makeQuery(id+"F3.opExtrude","CAP_FACE",FACE,{"disambiguationData":[OSD([subQ5,subQ1,subQ6,subQ7,subQ4,subQ3,subQ2,subQ0])],"isStart":false})})}),makeQuery(id+"F8.opExtrude","SWEPT_FACE",FACE,{"disambiguationData":[OSD([sQuery(id+"F7.wireOp",EDGE,"E67")])]})]});}
            var Q5;
            Q5=makeQuery(id+"F8.boolean.opBoolean","INTERSECT",EDGE,{"disambiguationData":[OD(0.0)],"derivedFrom":[makeQuery(id+"F5.opExtrude","SWEPT_FACE",FACE,{"disambiguationData":[OSD([sQuery(id+"F4.wireOp",EDGE,"E30")])]}),makeQuery(id+"F8.opExtrude","SWEPT_FACE",FACE,{"disambiguationData":[OSD([sQuery(id+"F7.wireOp",EDGE,"E67")])]})]});
            fillet(context, id + "F14", {"entities" : qUnion([Q0, Q1, Q2, Q3, Q4, Q5]), "radius" : 3 * mm, "tangentPropagation" : true, "allowEdgeOverflow" : false});
        }
        {
            var Q0;
            Q0=makeQuery(id+"F1.opExtrude","CAP_EDGE",EDGE,{"disambiguationData":[OSD([sQuery(id+"F0.wireOp",EDGE,"E1.bottom")])],"isStart":false});
            fillet(context, id + "F15", {"entities" : qUnion([Q0]), "radius" : 2 * mm, "tangentPropagation" : true, "allowEdgeOverflow" : false});
        }
        {
            var Q0;
            {var subQ0=sQuery(id+"F0.wireOp",EDGE,"E21.filletArc");var subQ1=sQuery(id+"F0.wireOp",EDGE,"E7");var subQ2=sQuery(id+"F0.wireOp",EDGE,"E6");var subQ3=sQuery(id+"F0.wireOp",EDGE,"E5");var subQ4=sQuery(id+"F0.wireOp",EDGE,"E4");var subQ5=sQuery(id+"F0.wireOp",EDGE,"E22.filletArc");var subQ6=sQuery(id+"F0.wireOp",EDGE,"E1.bottom");var subQ7=sQuery(id+"F0.wireOp",EDGE,"E1.right");var subQ8=sQuery(id+"F0.wireOp",EDGE,"E1.top");var subQ9=sQuery(id+"F0.wireOp",EDGE,"E1.left");var subQ10=sQuery(id+"F0.wireOp",EDGE,"E23.filletArc");var subQ11=sQuery(id+"F0.wireOp",EDGE,"E24.filletArc");Q0=makeQuery(id+"F2.boolean.opBoolean","SPLIT",FACE,{"disambiguationData":[TD([makeQuery(id+"F1.opExtrude","SWEPT_FACE",FACE,{"disambiguationData":[OSD([subQ6])]})])],"derivedFrom":makeQuery(id+"F1.opExtrude","CAP_FACE",FACE,{"disambiguationData":[OSD([subQ6,subQ8,subQ9,subQ7,subQ4,subQ3,subQ2,subQ1,subQ0,subQ5,subQ10,subQ11])],"isStart":true})});}
            var sketch = newSketch(context, id + "F16", { "sketchPlane" : qUnion([Q0])});
            skCircle(sketch, "E79", {"center": v(0, 104.7) * mm, "radius": 6.1 * mm});
            skLineSegment(sketch, "E80", {"start": v(-15, 104.7) * mm, "end": v(-15, 92.27) * mm});
            skLineSegment(sketch, "E81", {"start": v(-15, 92.27) * mm, "end": v(-30.01, 74.25) * mm});
            skLineSegment(sketch, "E82", {"start": v(15.02, 104.7) * mm, "end": v(15.02, 92.37) * mm});
            skLineSegment(sketch, "E83", {"start": v(15.02, 92.37) * mm, "end": v(30.04, 74.25) * mm});
            skArc(sketch, "E84", {"start": v(15.02, 104.7) * mm, "mid": v(0, 119.72) * mm, "end": v(-15, 104.7) * mm});
            skLineSegment(sketch, "E85", {"start": v(-64.25, 74.25) * mm, "end": v(64.25, 74.25) * mm});
            skLineSegment(sketch, "E86", {"start": v(-74.25, 64.25) * mm, "end": v(-74.25, -64.25) * mm});
            skLineSegment(sketch, "E87", {"start": v(74.25, 64.25) * mm, "end": v(74.25, -64.25) * mm});
            skLineSegment(sketch, "E88", {"start": v(-64.25, -74.25) * mm, "end": v(64.25, -74.25) * mm});
            skCircle(sketch, "E89", {"center": v(-60, 60) * mm, "radius": 3.99 * mm});
            skCircle(sketch, "E90", {"center": v(60, 60) * mm, "radius": 4.06 * mm});
            skCircle(sketch, "E91", {"center": v(60, -60) * mm, "radius": 3.93 * mm});
            skCircle(sketch, "E92", {"center": v(-60, -60) * mm, "radius": 3.96 * mm});
            skLineSegment(sketch, "E93", {"start": v(-60, -38.83) * mm, "end": v(-60, 38.83) * mm});
            skLineSegment(sketch, "E94", {"start": v(60, 38.83) * mm, "end": v(60, -38.83) * mm});
            skArc(sketch, "E95", {"start": v(-64.25, 74.25) * mm, "mid": v(-71.32, 71.32) * mm, "end": v(-74.25, 64.25) * mm});
            skArc(sketch, "E96", {"start": v(74.25, 64.25) * mm, "mid": v(71.32, 71.32) * mm, "end": v(64.25, 74.25) * mm});
            skArc(sketch, "E97", {"start": v(60, 38.83) * mm, "mid": v(58.44, 44.2) * mm, "end": v(54.26, 47.88) * mm});
            skArc(sketch, "E98", {"start": v(-74.25, -64.25) * mm, "mid": v(-71.32, -71.32) * mm, "end": v(-64.25, -74.25) * mm});
            skArc(sketch, "E99", {"start": v(64.25, -74.25) * mm, "mid": v(71.32, -71.32) * mm, "end": v(74.25, -64.25) * mm});
            skArc(sketch, "E100", {"start": v(74.25, -64.25) * mm, "mid": v(71.32, -71.32) * mm, "end": v(64.25, -74.25) * mm});
            skArc(sketch, "E101", {"start": v(-60, 38.83) * mm, "mid": v(-58.44, 44.2) * mm, "end": v(-54.26, 47.88) * mm});
            skArc(sketch, "E102", {"start": v(-54.26, 47.88) * mm, "mid": v(0, 60) * mm, "end": v(54.26, 47.88) * mm});
            skArc(sketch, "E103", {"start": v(60, -38.83) * mm, "mid": v(58.44, -44.2) * mm, "end": v(54.26, -47.88) * mm});
            skArc(sketch, "E104", {"start": v(54.26, -47.88) * mm, "mid": v(0, -60) * mm, "end": v(-54.26, -47.88) * mm});
            skArc(sketch, "E105", {"start": v(-54.26, -47.88) * mm, "mid": v(-58.44, -44.2) * mm, "end": v(-60, -38.83) * mm});
            skLineSegment(sketch, "E106", {"start": v(-74.25, 0) * mm, "end": v(74.25, 0) * mm, "construction": true});
            skLineSegment(sketch, "E107", {"start": v(74.25, 0) * mm, "end": v(74.25, 0) * mm});
            skLineSegment(sketch, "E108.MirrorCS", {"start": v(15.02, -92.37) * mm, "end": v(30.04, -74.25) * mm});
            skLineSegment(sketch, "E109.MirrorCS", {"start": v(-15, -92.27) * mm, "end": v(-30.01, -74.25) * mm});
            skLineSegment(sketch, "E110.MirrorCS", {"start": v(-15, -104.7) * mm, "end": v(-15, -92.27) * mm});
            skArc(sketch, "E111.MirrorCS", {"start": v(15.02, -104.7) * mm, "mid": v(0, -119.72) * mm, "end": v(-15, -104.7) * mm});
            skLineSegment(sketch, "E112.MirrorCS", {"start": v(15.02, -104.7) * mm, "end": v(15.02, -92.37) * mm});
            skCircle(sketch, "E113.MirrorC", {"center": v(0, -104.7) * mm, "radius": 6.1 * mm});
            skSolve(sketch);
        }
        {
            var Q0;
            Q0 = qSketchRegion(id + "F16", true);
            extrude(context, id + "F17", {"entities" : qUnion([Q0]), "depth" : 10.16 * mm, "offsetDistance" : 25.4 * mm});
        }
    });
